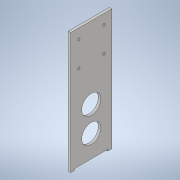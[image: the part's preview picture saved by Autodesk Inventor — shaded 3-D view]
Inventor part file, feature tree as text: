
AUTODESK INVENTOR PART (.ipt)
format: ipt  version: 2020 (Build 240168000, 168)  size: 140,288 bytes
history: native  units: mm
features: extrude x3, sketch x3, pattern_linear x1
ambient origin geometry x8: Origin, YZ Plane, XZ Plane, XY Plane, X Axis, Y Axis, Z Axis, Center Point
bodies: Body1 (feature_tree)
feature tree (7):
  extrude  "Extrusion3"  Depth=82.0mm
  extrude  "Extrusion4"  Depth=41.0mm
  extrude  "Extrusion5"  Depth=66.0mm
  pattern_linear  "Rectangular Pattern1"  Spacing1=3.0mm  [1 undecoded]
  sketch  "Sketch1"  dims[d0=241.0mm d1=82.0mm]
  sketch  "Sketch3"  dims[d2=38.0mm d3=41.0mm]
  sketch  "Sketch4"  dims[d4=174.0mm d5=66.0mm d6=3.0mm d7=8.0mm d22=5.0mm d23=0.0mm d24=5.0mm d25=5.0mm d26=20.0mm d28=50.0mm d29=20.0mm d31=50.0mm d34=82.0mm d35=16.0mm d36=19.5mm d37=5.0mm d38=0.0mm d39=38.0mm d40=44.0mm d41=5.0mm d42=0.0mm d43=20.0mm d45=50.0mm]
note: 1 required parameter value undecoded (feature->parameter linkage not recoverable at this tier; creation-order binding heuristic only, values carry confidence <= 0.55)
